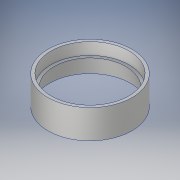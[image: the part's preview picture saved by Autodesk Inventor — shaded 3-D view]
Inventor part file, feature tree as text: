
AUTODESK INVENTOR PART (.ipt)
format: ipt  version: 2017 SP1 (Build 210196100, 196)  size: 160,768 bytes
history: native  units: in
note: dims shown in document units (in); Inventor stores cm internally (conversion verified against a paired STEP export)
features: revolve x1, sketch x1
ambient origin geometry x8: Origin, YZ Plane, XZ Plane, XY Plane, X Axis, Y Axis, Z Axis, Center Point
bodies: Solid1 (feature_tree)
feature tree (2):
  revolve  "Revolution1"  [1 undecoded]
  sketch  "Sketch1"  dims[d0=1.13in d1=3.75in d2=0.125in d3=0.1718in d5=1.0in d6=1.0in d7=90.0deg d8=0.5in d9=15.0deg d12=1.25in d13=0.25in d16=0.5in d17=0.5in d18=0.5in d19=2.5in d20=0.5in d22=0.375in d23=0.25in d25=0.234in d27=0.125in d28=0.25in d29=1.0in d30=4.25in d31=0.25in d33=0.8014in d34=15.0deg d35=0.125in d36=1.0in d37=90.0deg]
note: 1 required parameter value undecoded (feature->parameter linkage not recoverable at this tier; creation-order binding heuristic only, values carry confidence <= 0.55)
